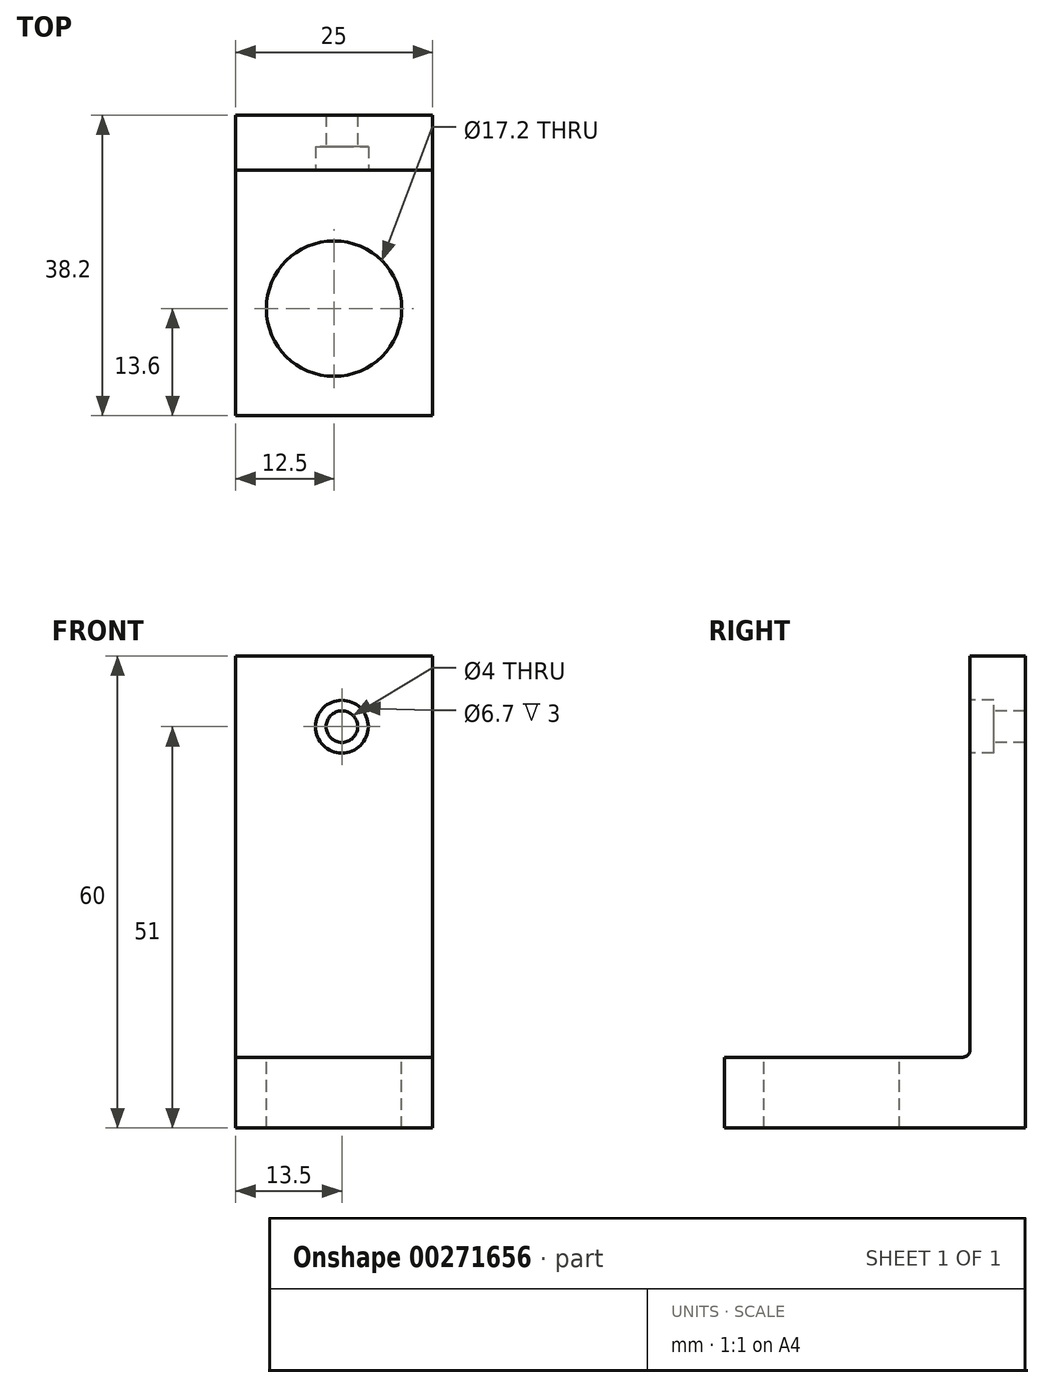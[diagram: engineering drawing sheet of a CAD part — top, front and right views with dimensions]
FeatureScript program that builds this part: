
annotation { "Feature Type Name" : "Feature", "Feature Type Description" : "" }
export const myFeature = defineFeature(function(context is Context, id is Id, definition is map)
    precondition{}
    {
        {
            var Q0;
            Q0=qCreatedBy(makeId("Right.planeOp"),FACE);
            var sketch = newSketch(context, id + "F0", { "sketchPlane" : qUnion([Q0])});
            skLineSegment(sketch, "E0.top", {"start": v(0, 0) * mm, "end": v(0, 0) * mm});
            skLineSegment(sketch, "E1", {"start": v(0, 0) * mm, "end": v(0, 60) * mm});
            skLineSegment(sketch, "E2", {"start": v(0, 60) * mm, "end": v(0, 0) * mm});
            skLineSegment(sketch, "E3.0", {"start": v(-7, 60) * mm, "end": v(-7, 0) * mm});
            skLineSegment(sketch, "E4", {"start": v(-7, 60) * mm, "end": v(0, 60) * mm});
            skLineSegment(sketch, "E5", {"start": v(-7, 0) * mm, "end": v(0, 0) * mm});
            skLineSegment(sketch, "E6", {"start": v(-7, 0) * mm, "end": v(-38.2, 0) * mm});
            skLineSegment(sketch, "E7.0", {"start": v(-7, 9) * mm, "end": v(-38.2, 9) * mm});
            skLineSegment(sketch, "E8", {"start": v(-38.2, 9) * mm, "end": v(-38.2, 0) * mm});
            skSolve(sketch);
        }
        {
            var Q0;
            Q0 = qSketchRegion(id + "F0", true);
            extrude(context, id + "F1", {"entities" : qUnion([Q0]), "oppositeDirection" : true, "depth" : 25 * mm});
        }
        {
            var Q0;
            Q0=makeQuery(id+"F1.opExtrude","SWEPT_FACE",FACE,{"disambiguationData":[OSD([sQuery(id+"F0.wireOp",EDGE,"E7.0")])]});
            var sketch = newSketch(context, id + "F2", { "sketchPlane" : qUnion([Q0])});
            skCircle(sketch, "E9", {"center": v(-12.5, -24.6) * mm, "radius": 8.6 * mm});
            skSolve(sketch);
        }
        {
            var Q0;
            Q0=sQuery(id+"F2.wireOp",VERTEX,"E9.center");
            var Q1;
            Q1=makeQuery(id+"F1.opExtrude","SWEPT_BODY",BODY,{"disambiguationData":[OSD([sQuery(id+"F0.wireOp",EDGE,"E2"),sQuery(id+"F0.wireOp",EDGE,"E3.0"),sQuery(id+"F0.wireOp",EDGE,"E4"),sQuery(id+"F0.wireOp",EDGE,"E5"),sQuery(id+"F0.wireOp",EDGE,"E6"),sQuery(id+"F0.wireOp",EDGE,"E7.0"),sQuery(id+"F0.wireOp",EDGE,"E8")])]});
            hole(context, id + "F3", {"style" : HoleStyle.SIMPLE, "endStyle" : HoleEndStyle.THROUGH, "holeDiameter" : 17.2 * mm, "tappedDepth" : 12 * mm, "tapClearance" : 3, "locations" : qUnion([Q0]), "scope" : qUnion([Q1])});
        }
        {
            var Q0;
            Q0=makeQuery(id+"F1.opExtrude","SWEPT_FACE",FACE,{"disambiguationData":[OSD([sQuery(id+"F0.wireOp",EDGE,"E3.0")])]});
            var sketch = newSketch(context, id + "F4", { "sketchPlane" : qUnion([Q0])});
            skCircle(sketch, "E10.cCircle", {"center": v(-11.5, 51) * mm, "radius": 1.74 * mm, "construction": true});
            skLineSegment(sketch, "E10.0", {"start": v(-10.5, 49.26) * mm, "end": v(-12.5, 49.26) * mm});
            skLineSegment(sketch, "E10.1", {"start": v(-12.5, 49.26) * mm, "end": v(-13.51, 51) * mm});
            skLineSegment(sketch, "E10.2", {"start": v(-13.51, 51) * mm, "end": v(-12.5, 52.74) * mm});
            skLineSegment(sketch, "E10.3", {"start": v(-12.5, 52.74) * mm, "end": v(-10.5, 52.74) * mm});
            skLineSegment(sketch, "E10.4", {"start": v(-10.5, 52.74) * mm, "end": v(-9.49, 51) * mm});
            skLineSegment(sketch, "E10.5", {"start": v(-9.49, 51) * mm, "end": v(-10.5, 49.26) * mm});
            skSolve(sketch);
        }
        {
            var Q0;
            Q0=sQuery(id+"F4.wireOp",VERTEX,"E10.cCircle.center");
            var Q1;
            Q1=makeQuery(id+"F1.opExtrude","SWEPT_BODY",BODY,{"disambiguationData":[OSD([sQuery(id+"F0.wireOp",EDGE,"E2"),sQuery(id+"F0.wireOp",EDGE,"E3.0"),sQuery(id+"F0.wireOp",EDGE,"E4"),sQuery(id+"F0.wireOp",EDGE,"E5"),sQuery(id+"F0.wireOp",EDGE,"E6"),sQuery(id+"F0.wireOp",EDGE,"E7.0"),sQuery(id+"F0.wireOp",EDGE,"E8")])]});
            hole(context, id + "F5", {"style" : HoleStyle.C_BORE, "endStyle" : HoleEndStyle.THROUGH, "holeDiameter" : 4 * mm, "cBoreDiameter" : 6.7 * mm, "cBoreDepth" : 3 * mm, "tappedDepth" : 12 * mm, "tapClearance" : 3, "startFromSketch" : true, "locations" : qUnion([Q0]), "scope" : qUnion([Q1])});
        }
        {
            var Q0;
            Q0=makeQuery(id+"F1.opExtrude","SWEPT_EDGE",EDGE,{"disambiguationData":[OSD([sQuery(id+"F0.wireOp",EDGE,"E3.0"),sQuery(id+"F0.wireOp",EDGE,"E7.0")])]});
            fillet(context, id + "F6", {"entities" : qUnion([Q0]), "radius" : 1 * mm, "tangentPropagation" : true, "allowEdgeOverflow" : false});
        }
    });
